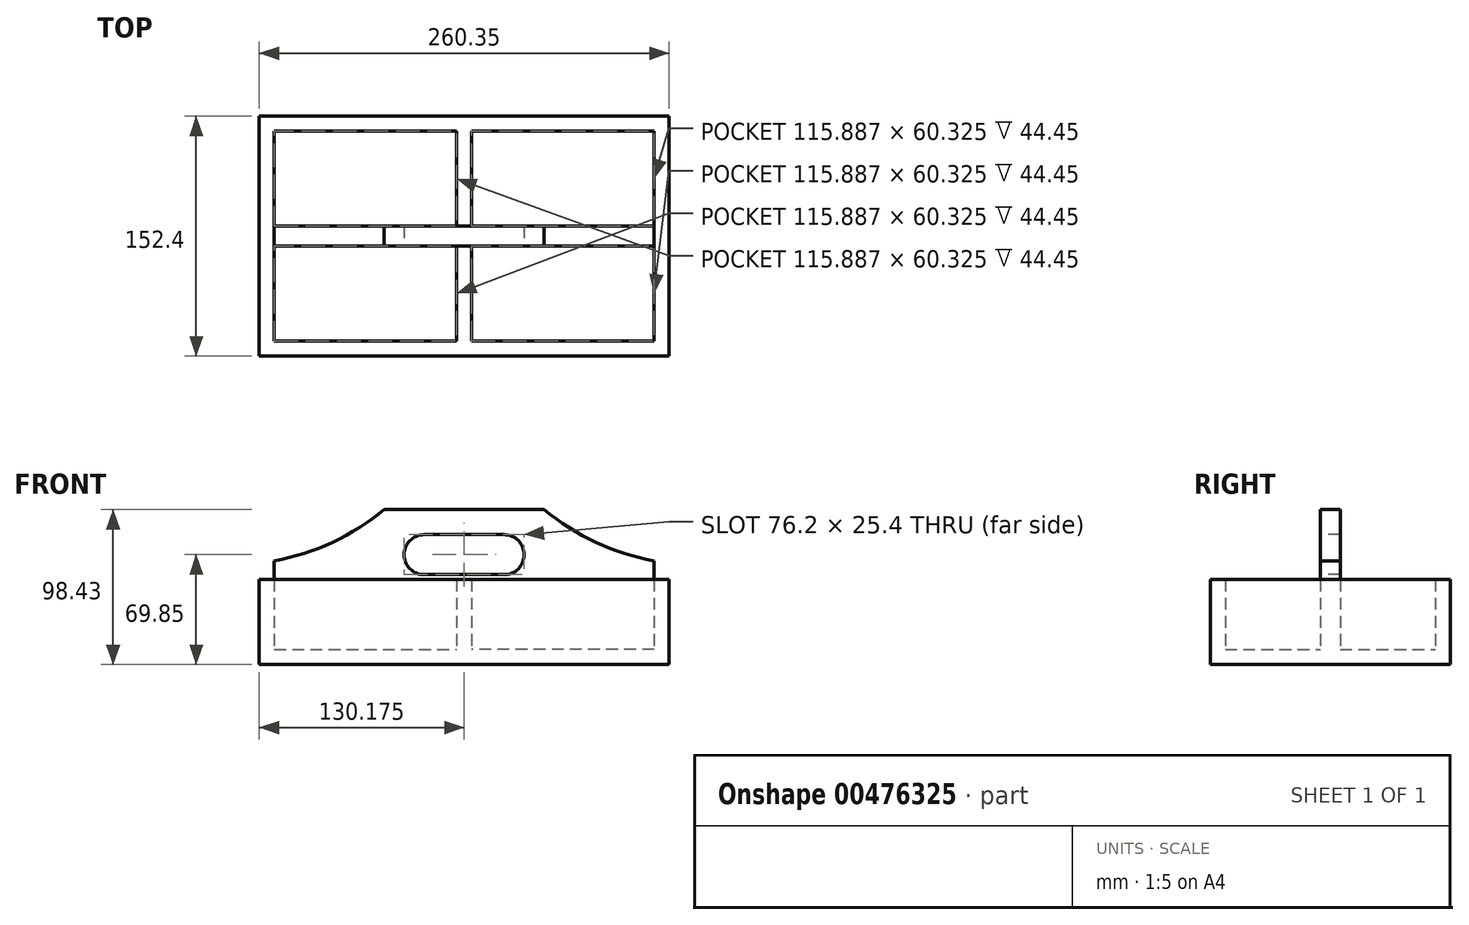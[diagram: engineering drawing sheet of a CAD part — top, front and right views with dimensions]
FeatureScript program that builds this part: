
annotation { "Feature Type Name" : "Feature", "Feature Type Description" : "" }
export const myFeature = defineFeature(function(context is Context, id is Id, definition is map)
    precondition{}
    {
        {
            var Q0;
            Q0=qCreatedBy(makeId("Front.planeOp"),FACE);
            var sketch = newSketch(context, id + "F0", { "sketchPlane" : qUnion([Q0])});
            skLineSegment(sketch, "E0", {"start": v(0, 0) * mm, "end": v(-260.35, 0) * mm});
            skLineSegment(sketch, "E1", {"start": v(-260.35, 0) * mm, "end": v(-260.35, 9.52) * mm});
            skLineSegment(sketch, "E2", {"start": v(-260.35, 9.52) * mm, "end": v(0, 9.53) * mm});
            skLineSegment(sketch, "E3", {"start": v(0, 9.53) * mm, "end": v(0, 0) * mm});
            skSolve(sketch);
        }
        {
            var Q0;
            Q0 = qSketchRegion(id + "F0", true);
            var Q1;
            Q1=makeQuery(id+"F0.imprint","IMPRINT",FACE,{"disambiguationData":[TD([[makeQuery(id+"F0.imprint","IMPRINT",EDGE,{"derivedFrom":sQuery(id+"F0.wireOp",EDGE,"E0")}),-1.0]])]});
            extrude(context, id + "F1", {"entities" : qUnion([Q0, Q1]), "depth" : 152.4 * mm});
        }
        {
            var Q0;
            Q0=makeQuery(id+"F1.opExtrude","SWEPT_FACE",FACE,{"disambiguationData":[OSD([sQuery(id+"F0.wireOp",EDGE,"E2")])]});
            var sketch = newSketch(context, id + "F2", { "sketchPlane" : qUnion([Q0])});
            skLineSegment(sketch, "E4", {"start": v(-250.83, -152.4) * mm, "end": v(-260.35, -152.4) * mm});
            skLineSegment(sketch, "E5", {"start": v(-260.35, -152.4) * mm, "end": v(-260.35, -142.87) * mm});
            skLineSegment(sketch, "E6", {"start": v(-260.35, -142.87) * mm, "end": v(0, -142.87) * mm});
            skLineSegment(sketch, "E7", {"start": v(0, -142.87) * mm, "end": v(0, -152.4) * mm});
            skLineSegment(sketch, "E8", {"start": v(0, -152.4) * mm, "end": v(-260.35, -152.4) * mm});
            skLineSegment(sketch, "E9", {"start": v(-260.35, 0) * mm, "end": v(-260.35, -9.52) * mm});
            skLineSegment(sketch, "E10", {"start": v(-260.35, -9.52) * mm, "end": v(0, -9.52) * mm});
            skLineSegment(sketch, "E11", {"start": v(0, -9.52) * mm, "end": v(0, 0) * mm});
            skLineSegment(sketch, "E12", {"start": v(0, 0) * mm, "end": v(-260.35, 0) * mm});
            skLineSegment(sketch, "E13", {"start": v(-260.35, -9.52) * mm, "end": v(-260.35, -142.87) * mm});
            skLineSegment(sketch, "E14", {"start": v(-248.47, -9.53) * mm, "end": v(-260.35, -9.52) * mm});
            skSolve(sketch);
        }
        {
            var Q0;
            Q0 = qSketchRegion(id + "F2", true);
            extrude(context, id + "F3", {"entities" : qUnion([Q0]), "operationType" : NewBodyOperationType.ADD, "depth" : 44.45 * mm});
        }
        {
            var Q0;
            Q0=makeQuery(id+"F1.opExtrude","SWEPT_FACE",FACE,{"disambiguationData":[OSD([sQuery(id+"F0.wireOp",EDGE,"E2")])]});
            var sketch = newSketch(context, id + "F4", { "sketchPlane" : qUnion([Q0])});
            skLineSegment(sketch, "E15", {"start": v(-260.35, -9.53) * mm, "end": v(-260.35, -142.87) * mm});
            skLineSegment(sketch, "E16", {"start": v(-260.35, -142.87) * mm, "end": v(-250.83, -142.87) * mm});
            skLineSegment(sketch, "E17", {"start": v(-250.83, -142.87) * mm, "end": v(-250.83, -9.53) * mm});
            skLineSegment(sketch, "E18", {"start": v(-250.83, -9.53) * mm, "end": v(-260.35, -9.52) * mm});
            skLineSegment(sketch, "E19", {"start": v(0, -9.53) * mm, "end": v(0, -142.87) * mm});
            skLineSegment(sketch, "E20", {"start": v(0, -142.87) * mm, "end": v(-9.53, -142.87) * mm});
            skLineSegment(sketch, "E21", {"start": v(-9.53, -142.87) * mm, "end": v(-9.53, -9.53) * mm});
            skLineSegment(sketch, "E22", {"start": v(-9.53, -9.53) * mm, "end": v(0, -9.53) * mm});
            skSolve(sketch);
        }
        {
            var Q0;
            Q0 = qSketchRegion(id + "F4", true);
            extrude(context, id + "F5", {"entities" : qUnion([Q0]), "operationType" : NewBodyOperationType.ADD, "depth" : 44.45 * mm});
        }
        {
            var Q0;
            Q0=makeQuery(id+"F1.opExtrude","SWEPT_FACE",FACE,{"disambiguationData":[OSD([sQuery(id+"F0.wireOp",EDGE,"E2")])]});
            var sketch = newSketch(context, id + "F6", { "sketchPlane" : qUnion([Q0])});
            skLineSegment(sketch, "E23", {"start": v(-250.83, -142.87) * mm, "end": v(-130.18, -142.87) * mm});
            skLineSegment(sketch, "E24", {"start": v(-250.83, -142.87) * mm, "end": v(-134.94, -142.87) * mm});
            skLineSegment(sketch, "E25", {"start": v(-134.94, -142.87) * mm, "end": v(-125.41, -142.87) * mm});
            skLineSegment(sketch, "E26", {"start": v(-125.41, -82.55) * mm, "end": v(-134.94, -82.55) * mm});
            skLineSegment(sketch, "E27", {"start": v(-134.94, -82.55) * mm, "end": v(-134.94, -142.87) * mm});
            skLineSegment(sketch, "E28", {"start": v(-125.41, -82.55) * mm, "end": v(-125.41, -142.87) * mm});
            skSolve(sketch);
        }
        {
            var Q0;
            Q0=makeQuery(id+"F6.imprint","IMPRINT",FACE,{"disambiguationData":[TD([[makeQuery(id+"F6.imprint","IMPRINT",EDGE,{"derivedFrom":sQuery(id+"F6.wireOp",EDGE,"E26")}),1.0]])]});
            extrude(context, id + "F7", {"entities" : qUnion([Q0]), "operationType" : NewBodyOperationType.ADD, "depth" : 44.45 * mm});
        }
        {
            var Q0;
            Q0=makeQuery(id+"F1.opExtrude","SWEPT_FACE",FACE,{"disambiguationData":[OSD([sQuery(id+"F0.wireOp",EDGE,"E2")])]});
            var sketch = newSketch(context, id + "F8", { "sketchPlane" : qUnion([Q0])});
            skLineSegment(sketch, "E29", {"start": v(-250.83, -82.55) * mm, "end": v(-9.53, -82.55) * mm});
            skLineSegment(sketch, "E30", {"start": v(-9.53, -82.55) * mm, "end": v(-9.53, -69.85) * mm});
            skLineSegment(sketch, "E31", {"start": v(-9.53, -69.85) * mm, "end": v(-250.83, -69.85) * mm});
            skLineSegment(sketch, "E32", {"start": v(-250.83, -69.85) * mm, "end": v(-250.83, -82.55) * mm});
            skSolve(sketch);
        }
        {
            var Q0;
            {var subQ0=sQuery(id+"F8.wireOp",EDGE,"E30");Q0=makeQuery(id+"F8.imprint","IMPRINT",FACE,{"disambiguationData":[TD([[makeQuery(id+"F8.imprint","IMPRINT",EDGE,{"derivedFrom":subQ0}),1.0]])]});}
            extrude(context, id + "F9", {"entities" : qUnion([Q0]), "operationType" : NewBodyOperationType.ADD, "depth" : 88.9 * mm});
        }
        {
            var Q0;
            Q0=makeQuery(id+"F9.opExtrude","SWEPT_FACE",FACE,{"disambiguationData":[OSD([sQuery(id+"F8.wireOp",EDGE,"E29")])]});
            var sketch = newSketch(context, id + "F10", { "sketchPlane" : qUnion([Q0])});
            skLineSegment(sketch, "E33", {"start": v(-250.83, 98.42) * mm, "end": v(-250.83, 63.5) * mm});
            skLineSegment(sketch, "E34", {"start": v(-250.83, 98.42) * mm, "end": v(-180.98, 98.42) * mm});
            skLineSegment(sketch, "E35", {"start": v(-250.83, 63.5) * mm, "end": v(-180.98, 63.5) * mm});
            skLineSegment(sketch, "E36", {"start": v(-9.53, 98.43) * mm, "end": v(-79.38, 98.42) * mm});
            skLineSegment(sketch, "E37", {"start": v(-79.38, 98.43) * mm, "end": v(-79.38, 63.5) * mm});
            skLineSegment(sketch, "E38", {"start": v(-79.38, 63.5) * mm, "end": v(-9.53, 63.5) * mm});
            skCircle(sketch, "E39", {"center": v(17.7, 215.9) * mm, "radius": 152.4 * mm});
            skCircle(sketch, "E40", {"center": v(-278.06, 215.9) * mm, "radius": 152.4 * mm});
            skSolve(sketch);
        }
        {
            var Q0;
            Q0 = qSketchRegion(id + "F10", true);
            extrude(context, id + "F11", {"entities" : qUnion([Q0]), "operationType" : NewBodyOperationType.ADD, "oppositeDirection" : true, "depth" : 25.4 * mm});
        }
        {
            var Q0;
            Q0 = qSketchRegion(id + "F10", true);
            extrude(context, id + "F12", {"entities" : qUnion([Q0]), "operationType" : NewBodyOperationType.REMOVE, "oppositeDirection" : true, "depth" : 25.4 * mm});
        }
        {
            var Q0;
            Q0=makeQuery(id+"F11.boolean.opBoolean","MERGE",FACE,{"derivedFrom":[makeQuery(id+"F9.opExtrude","SWEPT_FACE",FACE,{"disambiguationData":[OSD([sQuery(id+"F8.wireOp",EDGE,"E29")])]}),makeQuery(id+"F11.opExtrude","CAP_FACE",FACE,{"disambiguationData":[OSD([sQuery(id+"F10.wireOp",EDGE,"E39"),sQuery(id+"F10.wireOp",EDGE,"E40")])],"isStart":true})]});
            var sketch = newSketch(context, id + "F13", { "sketchPlane" : qUnion([Q0])});
            skLineSegment(sketch, "E41", {"start": v(-180.98, 98.42) * mm, "end": v(-155.58, 98.42) * mm});
            skLineSegment(sketch, "E42", {"start": v(-155.58, 98.42) * mm, "end": v(-155.58, 69.85) * mm});
            skArc(sketch, "E43", {"start": v(-155.58, 82.55) * mm, "mid": v(-168.28, 69.85) * mm, "end": v(-155.58, 57.15) * mm});
            skLineSegment(sketch, "E44", {"start": v(-79.38, 98.43) * mm, "end": v(-104.78, 98.43) * mm});
            skLineSegment(sketch, "E45", {"start": v(-104.78, 98.42) * mm, "end": v(-104.78, 69.85) * mm});
            skArc(sketch, "E46", {"start": v(-104.78, 57.15) * mm, "mid": v(-92.08, 69.85) * mm, "end": v(-104.78, 82.55) * mm});
            skLineSegment(sketch, "E47", {"start": v(-155.58, 82.55) * mm, "end": v(-104.78, 82.55) * mm});
            skLineSegment(sketch, "E48", {"start": v(-155.58, 57.15) * mm, "end": v(-104.78, 57.15) * mm});
            skSolve(sketch);
        }
        {
            var Q0;
            Q0 = qSketchRegion(id + "F13", true);
            extrude(context, id + "F14", {"entities" : qUnion([Q0]), "operationType" : NewBodyOperationType.REMOVE, "oppositeDirection" : true, "depth" : 12.7 * mm});
        }
        {
            var Q0;
            Q0=makeQuery(id+"F9.boolean.opBoolean","SPLIT",FACE,{"disambiguationData":[TD([makeQuery(id+"F9.opExtrude","SWEPT_FACE",FACE,{"disambiguationData":[OSD([sQuery(id+"F8.wireOp",EDGE,"E31")])]})])],"derivedFrom":makeQuery(id+"F1.opExtrude","SWEPT_FACE",FACE,{"disambiguationData":[OSD([sQuery(id+"F0.wireOp",EDGE,"E2")])]})});
            var sketch = newSketch(context, id + "F15", { "sketchPlane" : qUnion([Q0])});
            skLineSegment(sketch, "E49", {"start": v(-250.83, -9.53) * mm, "end": v(-134.94, -9.53) * mm});
            skLineSegment(sketch, "E50", {"start": v(-134.94, -9.53) * mm, "end": v(-134.94, -69.85) * mm});
            skLineSegment(sketch, "E51", {"start": v(-134.94, -69.85) * mm, "end": v(-125.41, -69.85) * mm});
            skLineSegment(sketch, "E52", {"start": v(-125.41, -69.85) * mm, "end": v(-125.41, -9.53) * mm});
            skLineSegment(sketch, "E53", {"start": v(-125.41, -9.53) * mm, "end": v(-9.53, -9.53) * mm});
            skSolve(sketch);
        }
        {
            var Q0;
            Q0 = qSketchRegion(id + "F15", true);
            var Q1;
            {var subQ0=sQuery(id+"F15.wireOp",EDGE,"E50");Q1=makeQuery(id+"F15.imprint","IMPRINT",FACE,{"disambiguationData":[TD([[makeQuery(id+"F15.imprint","IMPRINT",EDGE,{"derivedFrom":subQ0}),1.0]])]});}
            extrude(context, id + "F16", {"entities" : qUnion([Q0, Q1]), "operationType" : NewBodyOperationType.ADD, "depth" : 44.45 * mm});
        }
    });
